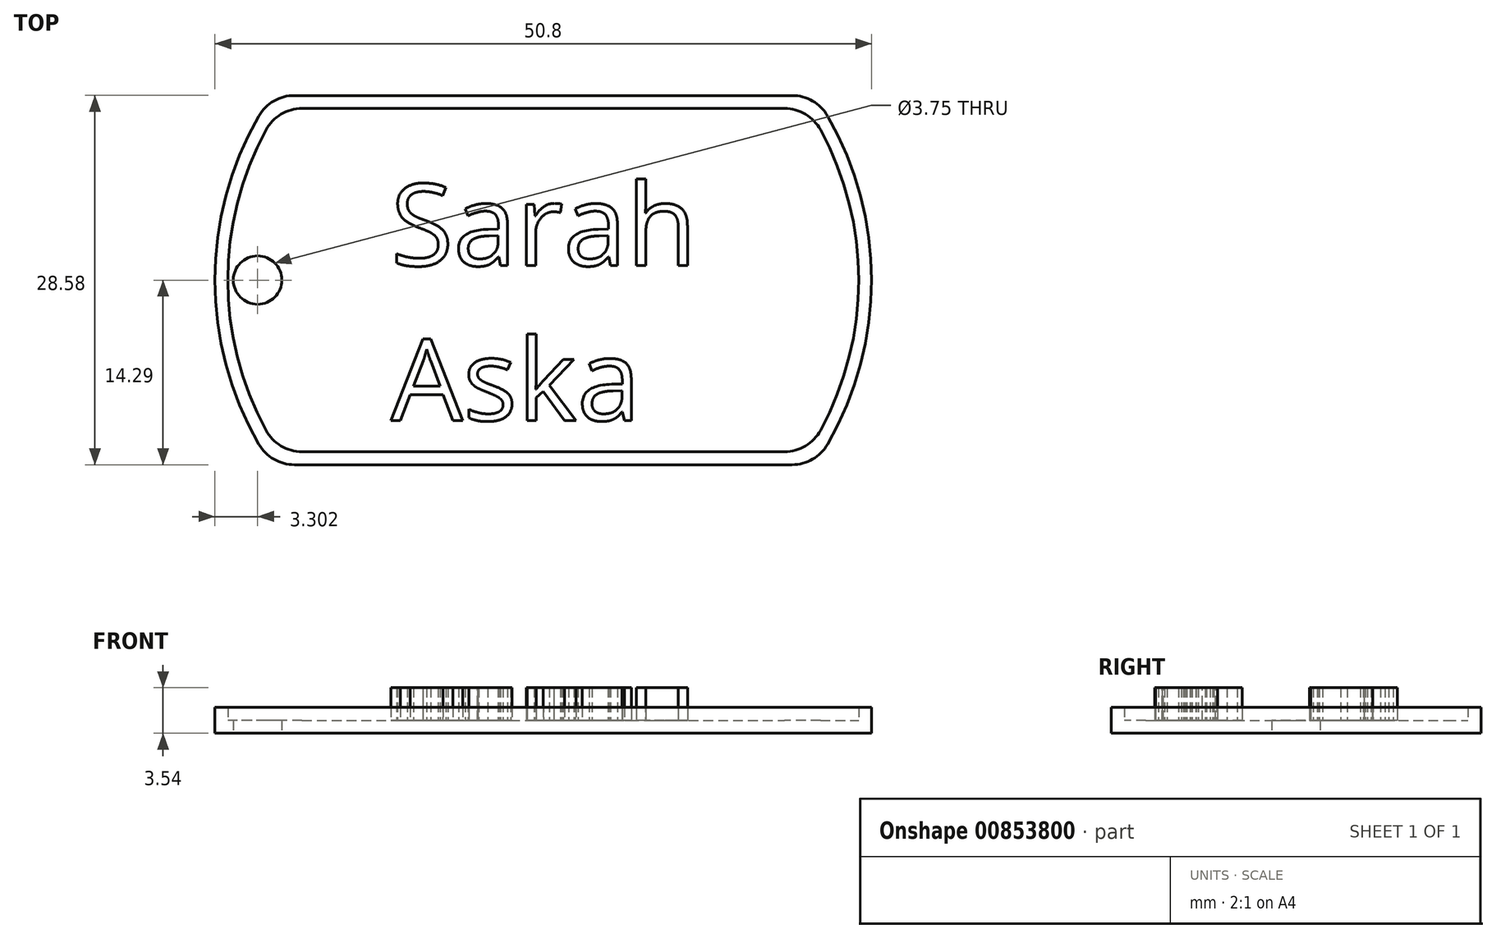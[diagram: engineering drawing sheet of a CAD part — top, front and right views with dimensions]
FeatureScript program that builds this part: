
annotation { "Feature Type Name" : "Feature", "Feature Type Description" : "" }
export const myFeature = defineFeature(function(context is Context, id is Id, definition is map)
    precondition{}
    {
        {
            var Q0;
            Q0=qCreatedBy(makeId("Top.planeOp"),FACE);
            var sketch = newSketch(context, id + "F0", { "sketchPlane" : qUnion([Q0])});
            skArc(sketch, "E0", {"start": v(-22, 12.7) * mm, "mid": v(-25.4, 0) * mm, "end": v(-22, -12.7) * mm});
            skLineSegment(sketch, "E1.top", {"start": v(-19.25, -14.29) * mm, "end": v(19.25, -14.29) * mm});
            skArc(sketch, "E2.trimOffspring", {"start": v(22, -12.7) * mm, "mid": v(25.4, 0) * mm, "end": v(22, 12.7) * mm});
            skLineSegment(sketch, "E3", {"start": v(-19.25, 14.29) * mm, "end": v(19.25, 14.29) * mm});
            skPoint(sketch, "E4.visualSharp", {"position": v(-21, 14.29) * mm});
            skArc(sketch, "E4.filletArc", {"start": v(-19.25, 14.29) * mm, "mid": v(-20.83, 13.86) * mm, "end": v(-22, 12.7) * mm});
            skPoint(sketch, "E5.visualSharp", {"position": v(21, 14.29) * mm});
            skArc(sketch, "E5.filletArc", {"start": v(22, 12.7) * mm, "mid": v(20.83, 13.86) * mm, "end": v(19.25, 14.29) * mm});
            skPoint(sketch, "E6.visualSharp", {"position": v(21, -14.29) * mm});
            skArc(sketch, "E6.filletArc", {"start": v(19.25, -14.29) * mm, "mid": v(20.83, -13.86) * mm, "end": v(22, -12.7) * mm});
            skPoint(sketch, "E7.visualSharp", {"position": v(-21, -14.29) * mm});
            skArc(sketch, "E7.filletArc", {"start": v(-22, -12.7) * mm, "mid": v(-20.83, -13.86) * mm, "end": v(-19.25, -14.29) * mm});
            skCircle(sketch, "E8", {"center": v(-22.1, 0) * mm, "radius": 1.87 * mm});
            skSolve(sketch);
        }
        {
            var Q0;
            Q0=makeQuery(id+"F0.imprint","IMPRINT",FACE,{"disambiguationData":[TD([[makeQuery(id+"F0.imprint","IMPRINT",EDGE,{"derivedFrom":sQuery(id+"F0.wireOp",EDGE,"E0")}),1.0]])]});
            extrude(context, id + "F1", {"entities" : qUnion([Q0]), "depth" : 1 * mm, "offsetDistance" : 25.4 * mm});
        }
        {
            var Q0;
            Q0=makeQuery(id+"F1.opExtrude","CAP_FACE",FACE,{"disambiguationData":[OSD([sQuery(id+"F0.wireOp",EDGE,"E0"),sQuery(id+"F0.wireOp",EDGE,"E1.top"),sQuery(id+"F0.wireOp",EDGE,"E2.trimOffspring"),sQuery(id+"F0.wireOp",EDGE,"E3"),sQuery(id+"F0.wireOp",EDGE,"E4.filletArc"),sQuery(id+"F0.wireOp",EDGE,"E5.filletArc"),sQuery(id+"F0.wireOp",EDGE,"E6.filletArc"),sQuery(id+"F0.wireOp",EDGE,"E7.filletArc")])],"isStart":false});
            var sketch = newSketch(context, id + "F2", { "sketchPlane" : qUnion([Q0])});
            skLineSegment(sketch, "E9.0", {"start": v(-18.66, 13.29) * mm, "end": v(18.66, 13.29) * mm});
            skArc(sketch, "E9.1", {"start": v(-21.45, 11.63) * mm, "mid": v(-24.4, 0) * mm, "end": v(-21.45, -11.63) * mm});
            skLineSegment(sketch, "E9.2", {"start": v(-18.66, -13.29) * mm, "end": v(18.66, -13.29) * mm});
            skArc(sketch, "E9.3", {"start": v(21.45, -11.63) * mm, "mid": v(24.4, 0) * mm, "end": v(21.45, 11.63) * mm});
            skPoint(sketch, "E10.visualSharp", {"position": v(-20.46, 13.29) * mm});
            skArc(sketch, "E10.filletArc", {"start": v(-18.66, 13.29) * mm, "mid": v(-20.29, 12.84) * mm, "end": v(-21.45, 11.63) * mm});
            skPoint(sketch, "E11.visualSharp", {"position": v(20.46, 13.29) * mm});
            skArc(sketch, "E11.filletArc", {"start": v(21.45, 11.63) * mm, "mid": v(20.29, 12.84) * mm, "end": v(18.66, 13.29) * mm});
            skPoint(sketch, "E12.visualSharp", {"position": v(20.46, -13.29) * mm});
            skArc(sketch, "E12.filletArc", {"start": v(18.66, -13.29) * mm, "mid": v(20.29, -12.84) * mm, "end": v(21.45, -11.63) * mm});
            skPoint(sketch, "E13.visualSharp", {"position": v(-20.46, -13.29) * mm});
            skArc(sketch, "E13.filletArc", {"start": v(-21.45, -11.63) * mm, "mid": v(-20.29, -12.84) * mm, "end": v(-18.66, -13.29) * mm});
            skLineSegment(sketch, "E14.0", {"start": v(-19.25, 14.29) * mm, "end": v(19.25, 14.29) * mm});
            skArc(sketch, "E14.1", {"start": v(-22, 12.7) * mm, "mid": v(-25.4, 0) * mm, "end": v(-22, -12.7) * mm});
            skLineSegment(sketch, "E14.2", {"start": v(-19.25, -14.29) * mm, "end": v(19.25, -14.29) * mm});
            skArc(sketch, "E14.3", {"start": v(22, -12.7) * mm, "mid": v(25.4, 0) * mm, "end": v(22, 12.7) * mm});
            skPoint(sketch, "E15.visualSharp", {"position": v(-21, -14.29) * mm});
            skArc(sketch, "E15.filletArc", {"start": v(-22, -12.7) * mm, "mid": v(-20.83, -13.86) * mm, "end": v(-19.25, -14.29) * mm});
            skPoint(sketch, "E16.visualSharp", {"position": v(21, -14.29) * mm});
            skArc(sketch, "E16.filletArc", {"start": v(19.25, -14.29) * mm, "mid": v(20.83, -13.86) * mm, "end": v(22, -12.7) * mm});
            skPoint(sketch, "E17.visualSharp", {"position": v(21, 14.29) * mm});
            skArc(sketch, "E17.filletArc", {"start": v(22, 12.7) * mm, "mid": v(20.83, 13.86) * mm, "end": v(19.25, 14.29) * mm});
            skPoint(sketch, "E18.visualSharp", {"position": v(-21, 14.29) * mm});
            skArc(sketch, "E18.filletArc", {"start": v(-19.25, 14.29) * mm, "mid": v(-20.83, 13.86) * mm, "end": v(-22, 12.7) * mm});
            skSolve(sketch);
        }
        {
            var Q0;
            Q0=makeQuery(id+"F2.imprint","IMPRINT",FACE,{"disambiguationData":[TD([[makeQuery(id+"F2.imprint","IMPRINT",EDGE,{"derivedFrom":sQuery(id+"F2.wireOp",EDGE,"E9.0")}),1.0]])]});
            extrude(context, id + "F3", {"entities" : qUnion([Q0]), "operationType" : NewBodyOperationType.ADD, "depth" : 1 * mm, "offsetDistance" : 25.4 * mm});
        }
        {
            var Q0;
            Q0=makeQuery(id+"F1.opExtrude","CAP_FACE",FACE,{"disambiguationData":[OSD([sQuery(id+"F0.wireOp",EDGE,"E0"),sQuery(id+"F0.wireOp",EDGE,"E1.top"),sQuery(id+"F0.wireOp",EDGE,"E2.trimOffspring"),sQuery(id+"F0.wireOp",EDGE,"E3"),sQuery(id+"F0.wireOp",EDGE,"E4.filletArc"),sQuery(id+"F0.wireOp",EDGE,"E5.filletArc"),sQuery(id+"F0.wireOp",EDGE,"E6.filletArc"),sQuery(id+"F0.wireOp",EDGE,"E7.filletArc"),sQuery(id+"F0.wireOp",EDGE,"E8")])],"isStart":false});
            var sketch = newSketch(context, id + "F4", { "sketchPlane" : qUnion([Q0])});
            skText(sketch, "E19", { "text": "Sarah\nAska", "fontName": "OpenSans-Regular.ttf"});
            const initialGuessF4  = {"E19": [-0.0118, 0.00113, 1, 0, 0.00635]};
            skSetInitialGuess(sketch, initialGuessF4);
            skSolve(sketch);
        }
        {
            var Q0;
            Q0 = qSketchRegion(id + "F4", true);
            extrude(context, id + "F5", {"entities" : qUnion([Q0]), "operationType" : NewBodyOperationType.ADD, "depth" : 2.54 * mm, "offsetDistance" : 25.4 * mm});
        }
    });
